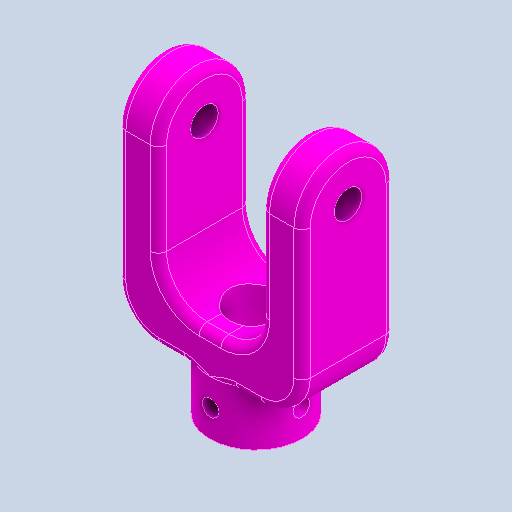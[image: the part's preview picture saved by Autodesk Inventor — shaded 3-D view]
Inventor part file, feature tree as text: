
AUTODESK INVENTOR PART (.ipt)
format: ipt  version: 2022 (Build 260153000, 153)  size: 291,328 bytes
history: native  units: in
note: dims shown in document units (in); Inventor stores cm internally (conversion verified against a paired STEP export)
features: sketch x5, other x4, plane x1
ambient origin geometry x8: Origin, YZ Plane, XZ Plane, XY Plane, X Axis, Y Axis, Z Axis, Center Point
bodies: Solid1 (feature_tree)
feature tree (10):
  other  "fork.ipt"
  other  "Solid1::fork.ipt"
  other  "TaggingFeature1"
  sketch  "Sketch1"  dims[d0=0.3937in]
  sketch  "Sketch2"
  sketch  "Sketch3"
  sketch  "Sketch4"
  sketch  "Sketch5"
  plane  "Work Plane1"
  other  "Work Axis1"
